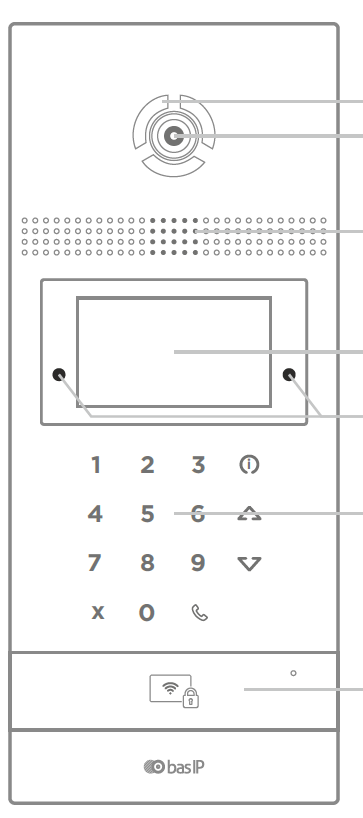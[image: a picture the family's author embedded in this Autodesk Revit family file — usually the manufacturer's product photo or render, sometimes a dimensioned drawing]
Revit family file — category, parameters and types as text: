
# Revit family: BAS-IP_Вызывная панель_AA-12FBI
name_source: partatom
category: Устройства связи
units: mm (PartAtom-declared; Revit-internal decimal feet)

## family parameters
Всегда вертикально = Да
На основе рабочей плоскости = Нет
Общий = Нет
При загрузке вырезать с полостями = Нет
Размер круглого соединителя = Использовать диаметр
Сохранять ориентацию аннотаций = Нет
Тип детали = Нормальный
Точка расчета площади = Нет

## types (2) — shared parameters
ADSK_Единица измерения = шт.
ADSK_Завод-изготовитель = BAS-IP
ADSK_Количество = 1
ADSK_Наименование = Многоабонентская IP вызывная панель
IK-код = IK07
Выходное видео = Full HD (1920 × 1080), H.264 Main Profile
Дисплей = 4,3” TFT, цветной с подсветкой
Изготовитель = BAS-IP
Камера = 1/3”
Класс степени защиты = IP65
Корпус = Алюминий
Минимальная освещенность = 0,01 Люкс
Ночная подсветка = 6 светодиодов
Питание = +12 В постоянного тока
Потребление питания = 6,5 Вт, в режиме ожидания - 3,6 Вт
Размер под установку = 142 × 358 × 58 мм
Размер самой панели = 161 × 382 × 49 мм
Разрешение = 2 Мп
Температурный режим = -40 – +65 °С
Тип клавиатуры = Пьезоэлектрические кнопки с подсветкой
Тип панели = Многоабонентская
Тип установки = Скрытого монтажа, накладной с BR-AA12
Угол обзора камеры = 110° (по горизонтали)

## per-type parameters (varying)
| type | ADSK_Марка | ADSK_Материал | Цвет |
| Серебристый | AA-12FBI Silver | Silver | Gray silver |
| Черный | AA-12FBI Black | Black silver | Black silver 2 |

note: column(s) folded — value = type name in every type: Цветовое решение
